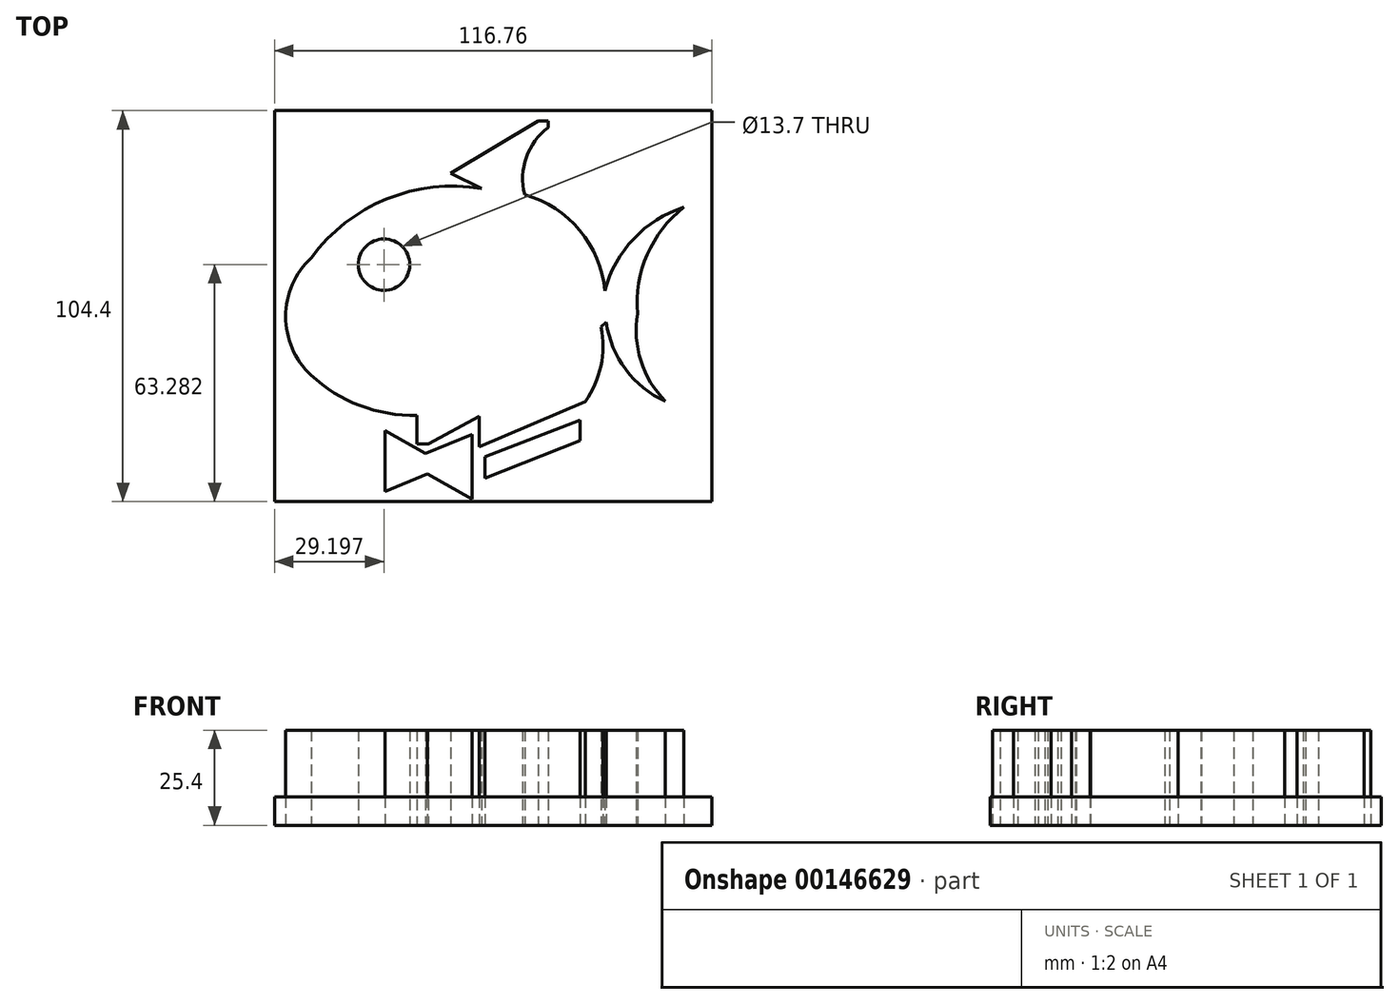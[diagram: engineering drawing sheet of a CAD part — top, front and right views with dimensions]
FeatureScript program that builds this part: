
annotation { "Feature Type Name" : "Feature", "Feature Type Description" : "" }
export const myFeature = defineFeature(function(context is Context, id is Id, definition is map)
    precondition{}
    {
        {
            var Q0;
            Q0=qCreatedBy(makeId("Top.planeOp"),FACE);
            var sketch = newSketch(context, id + "F0", { "sketchPlane" : qUnion([Q0])});
            skArc(sketch, "E0", {"start": v(-48.62, 12.89) * mm, "mid": v(-55.44, -2.73) * mm, "end": v(-48.73, -18.4) * mm});
            skArc(sketch, "E1", {"start": v(-48.73, -18.4) * mm, "mid": v(-35.6, -26.56) * mm, "end": v(-20.37, -29.12) * mm});
            skArc(sketch, "E2", {"start": v(-3.15, 31.4) * mm, "mid": v(-28.51, 28.6) * mm, "end": v(-48.62, 12.89) * mm});
            skLineSegment(sketch, "E3", {"start": v(-20.37, -29.12) * mm, "end": v(-20.37, -36.82) * mm});
            skLineSegment(sketch, "E4", {"start": v(-20.37, -36.82) * mm, "end": v(-17.38, -36.82) * mm});
            skLineSegment(sketch, "E5", {"start": v(-17.38, -36.82) * mm, "end": v(-3.8, -29.48) * mm});
            skLineSegment(sketch, "E6", {"start": v(-3.8, -29.48) * mm, "end": v(-3.8, -37.52) * mm});
            skLineSegment(sketch, "E7", {"start": v(-3.8, -37.52) * mm, "end": v(24.53, -25.42) * mm});
            skArc(sketch, "E8", {"start": v(24.53, -25.42) * mm, "mid": v(28.71, -15.95) * mm, "end": v(28.77, -5.6) * mm});
            skArc(sketch, "E9", {"start": v(30.16, -4.3) * mm, "mid": v(35.32, -16.89) * mm, "end": v(45.93, -25.41) * mm});
            skArc(sketch, "E10", {"start": v(38.53, -1.98) * mm, "mid": v(39.37, -14.6) * mm, "end": v(45.93, -25.41) * mm});
            skArc(sketch, "E11", {"start": v(50.89, 26.4) * mm, "mid": v(41.09, 13.8) * mm, "end": v(38.53, -1.98) * mm});
            skArc(sketch, "E12", {"start": v(50.89, 26.4) * mm, "mid": v(37.45, 18) * mm, "end": v(29.78, 4.13) * mm});
            skLineSegment(sketch, "E13", {"start": v(28.77, -5.6) * mm, "end": v(30.16, -4.3) * mm});
            skArc(sketch, "E14", {"start": v(29.78, 4.13) * mm, "mid": v(23.04, 20.24) * mm, "end": v(8.38, 29.73) * mm});
            skLineSegment(sketch, "E15", {"start": v(-3.15, 31.4) * mm, "end": v(-11.37, 35.48) * mm});
            skLineSegment(sketch, "E16", {"start": v(-11.37, 35.48) * mm, "end": v(12, 49.49) * mm});
            skLineSegment(sketch, "E17", {"start": v(12, 49.49) * mm, "end": v(14.69, 49.49) * mm});
            skLineSegment(sketch, "E18", {"start": v(14.69, 49.49) * mm, "end": v(14.69, 47.73) * mm});
            skArc(sketch, "E19", {"start": v(14.69, 47.73) * mm, "mid": v(8.79, 39.7) * mm, "end": v(8.38, 29.73) * mm});
            skCircle(sketch, "E20", {"center": v(-29.18, 11.08) * mm, "radius": 6.85 * mm});
            skLineSegment(sketch, "E21", {"start": v(-18.07, -39.29) * mm, "end": v(-5.66, -34.18) * mm});
            skLineSegment(sketch, "E22", {"start": v(-5.66, -34.18) * mm, "end": v(-5.66, -51.48) * mm});
            skLineSegment(sketch, "E23", {"start": v(-5.66, -51.48) * mm, "end": v(-17.57, -44.82) * mm});
            skLineSegment(sketch, "E24", {"start": v(-17.57, -44.82) * mm, "end": v(-28.88, -49.48) * mm});
            skLineSegment(sketch, "E25", {"start": v(-28.88, -49.48) * mm, "end": v(-28.88, -33.24) * mm});
            skLineSegment(sketch, "E26", {"start": v(-28.88, -33.24) * mm, "end": v(-18.07, -39.29) * mm});
            skLineSegment(sketch, "E27", {"start": v(-2.22, -40.25) * mm, "end": v(23.14, -30.42) * mm});
            skLineSegment(sketch, "E28", {"start": v(23.14, -30.42) * mm, "end": v(23.14, -35.87) * mm});
            skLineSegment(sketch, "E29", {"start": v(23.14, -35.87) * mm, "end": v(-2.22, -45.89) * mm});
            skLineSegment(sketch, "E30", {"start": v(-2.22, -45.89) * mm, "end": v(-2.22, -40.25) * mm});
            skSolve(sketch);
        }
        {
            var Q0;
            Q0=makeQuery(id+"F0.imprint","IMPRINT",FACE,{"disambiguationData":[TD([[makeQuery(id+"F0.imprint","IMPRINT",EDGE,{"derivedFrom":sQuery(id+"F0.wireOp",EDGE,"E0")}),1.0]])]});
            var Q1;
            Q1=makeQuery(id+"F0.imprint","IMPRINT",FACE,{"disambiguationData":[TD([[makeQuery(id+"F0.imprint","IMPRINT",EDGE,{"derivedFrom":sQuery(id+"F0.wireOp",EDGE,"E21")}),-1.0]])]});
            var Q2;
            Q2=makeQuery(id+"F0.imprint","IMPRINT",FACE,{"disambiguationData":[TD([[makeQuery(id+"F0.imprint","IMPRINT",EDGE,{"derivedFrom":sQuery(id+"F0.wireOp",EDGE,"E27")}),-1.0]])]});
            extrude(context, id + "F1", {"entities" : qUnion([Q0, Q1, Q2]), "depth" : 25.4 * mm});
        }
        {
            var Q0;
            Q0=qCreatedBy(makeId("Top.planeOp"),FACE);
            var sketch = newSketch(context, id + "F2", { "sketchPlane" : qUnion([Q0])});
            skLineSegment(sketch, "E31.bottom", {"start": v(58.38, -52.2) * mm, "end": v(-58.38, -52.2) * mm});
            skLineSegment(sketch, "E31.top", {"start": v(58.38, 52.2) * mm, "end": v(-58.38, 52.2) * mm});
            skLineSegment(sketch, "E31.left", {"start": v(58.38, -52.2) * mm, "end": v(58.38, 52.2) * mm});
            skLineSegment(sketch, "E31.right", {"start": v(-58.38, -52.2) * mm, "end": v(-58.38, 52.2) * mm});
            skPoint(sketch, "E31.middle", {"position": v(0, 0) * mm});
            skSolve(sketch);
        }
        {
            var Q0;
            Q0 = qSketchRegion(id + "F2", true);
            extrude(context, id + "F3", {"entities" : qUnion([Q0]), "depth" : 7.62 * mm});
        }
    });
